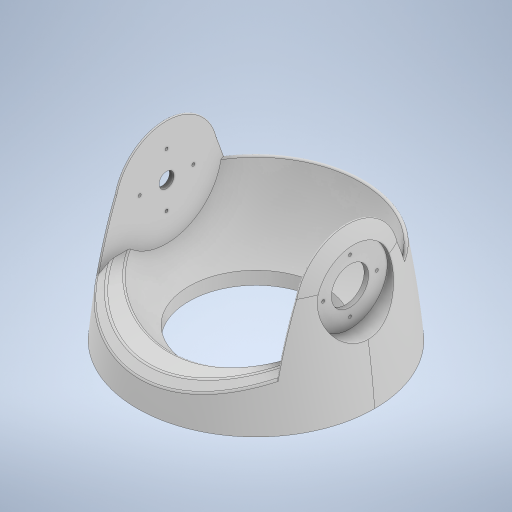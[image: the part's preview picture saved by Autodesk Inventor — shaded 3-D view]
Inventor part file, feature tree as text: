
AUTODESK INVENTOR PART (.ipt)
format: ipt  version: 2023 (Build 270158000, 158)  size: 777,216 bytes
history: native  units: mm
features: sketch x18, extrude x16, fillet x4, other x3, revolve x3, chamfer x3, mirror x2, projected_geometry x2, pattern_circular x1, hole x1
ambient origin geometry x8: Origin, YZ Plane, XZ Plane, XY Plane, X Axis, Y Axis, Z Axis, Center Point
bodies: Body1 (feature_tree)
feature tree (53):
  other  "솔리드1"
  revolve  "회전1"
  sketch  "스케치2"
  revolve  "회전2"
  revolve  "회전3"
  extrude  "돌출3"  Depth=120.0mm
  extrude  "돌출4"  Depth=140.0mm
  chamfer  "모따기1"  Distance=60.0mm
  fillet  "모깎기1"  Radius=130.0mm
  extrude  "돌출5"  Depth=160.0mm
  fillet  "모깎기2"  [1 undecoded]
  fillet  "모깎기3"  Radius=120.0mm
  extrude  "돌출6"  Depth=141.0mm
  other  "작업 평면2"
  extrude  "돌출7"  TaperAngle=90.0deg  [1 undecoded]
  mirror  "미러1"
  extrude  "돌출9"  Depth=4.0mm
  extrude  "돌출10"  TaperAngle=90.0deg  [1 undecoded]
  mirror  "미러2"
  sketch  "스케치13"
  extrude  "돌출11"  Depth=10.0mm
  extrude  "돌출12"  Depth=371.75mm TaperAngle=0.0deg
  sketch  "스케치15"
  extrude  "돌출13"  Depth=25.0mm
  extrude  "돌출14"  Depth=140.0mm
  pattern_circular  "원형 패턴1"  [2 undecoded]
  extrude  "돌출15"  Depth=103.5mm TaperAngle=0.0deg
  fillet  "모깎기4"  Radius=5.0mm
  other  "작업 평면4"
  extrude  "돌출16"  Depth=2.0mm
  chamfer  "모따기2"  Distance=90.0mm
  extrude  "돌출17"  Depth=103.5mm TaperAngle=0.0deg
  chamfer  "모따기3"  Distance=1.0mm
  extrude  "돌출18"  Depth=0.5mm
  extrude  "돌출19"  Depth=7.0mm TaperAngle=0.0deg
  hole  "구멍1"  [1 undecoded]
  sketch  "스케치1"
  sketch  "스케치3"
  projected_geometry  "투영된 루프1"
  sketch  "스케치5"
  sketch  "스케치6"
  sketch  "스케치7"
  sketch  "스케치8"
  projected_geometry  "투영된 루프2"
  sketch  "스케치9"
  sketch  "스케치11"
  sketch  "스케치12"
  sketch  "스케치16"
  sketch  "스케치17"
  sketch  "스케치18"
  sketch  "스케치20"
  sketch  "스케치21"
  sketch  "스케치22"
note: 6 required parameter values undecoded (feature->parameter linkage not recoverable at this tier; creation-order binding heuristic only, values carry confidence <= 0.55)
